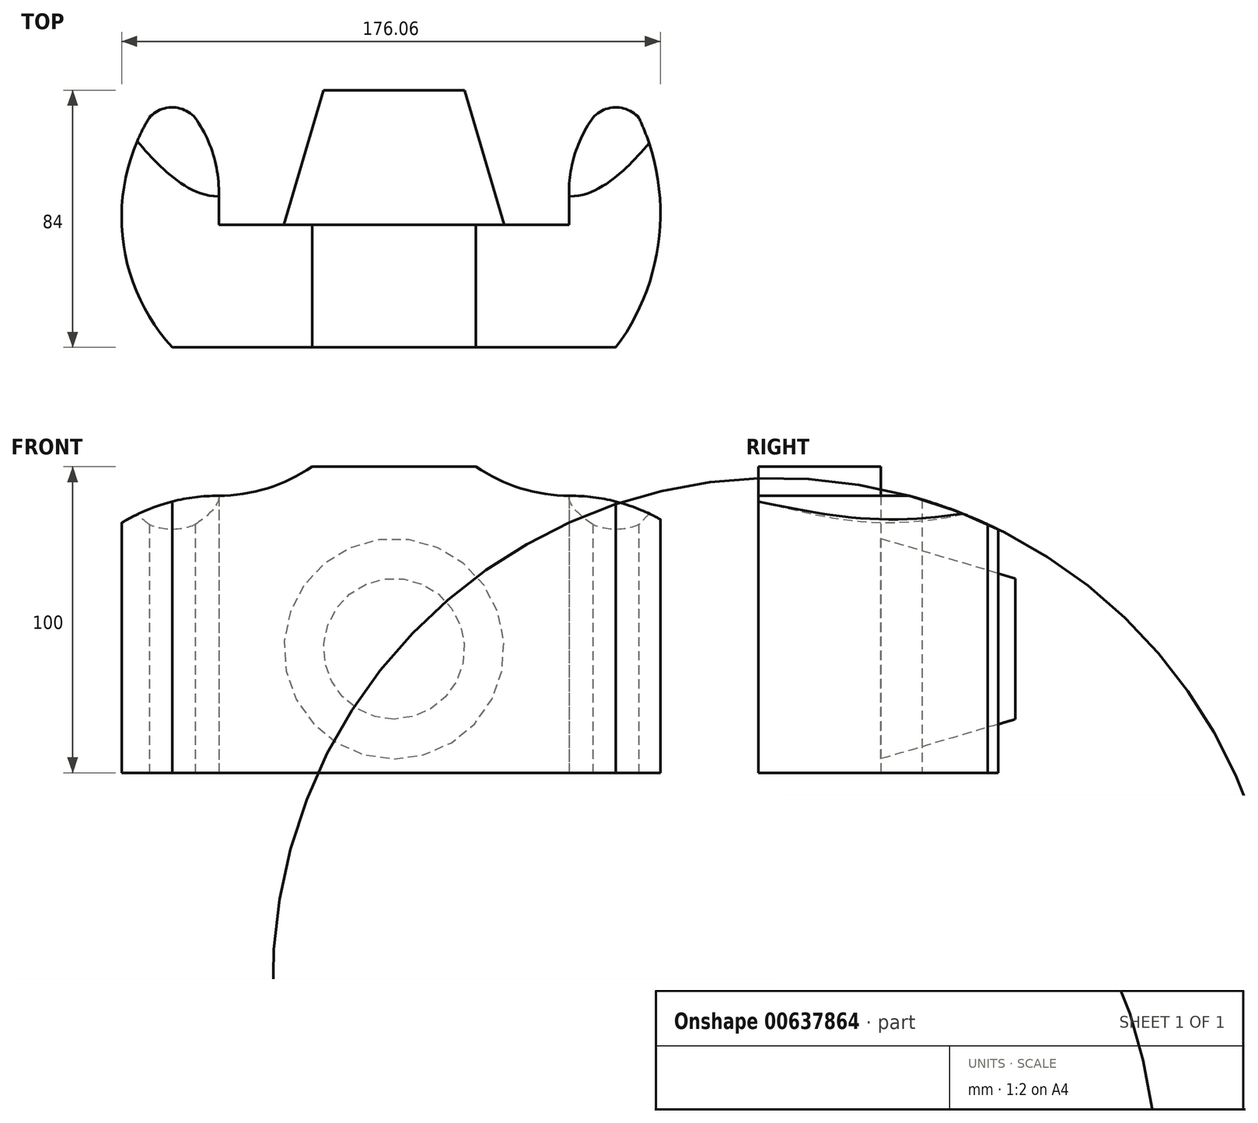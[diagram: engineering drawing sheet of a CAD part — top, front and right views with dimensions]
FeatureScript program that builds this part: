
annotation { "Feature Type Name" : "Feature", "Feature Type Description" : "" }
export const myFeature = defineFeature(function(context is Context, id is Id, definition is map)
    precondition{}
    {
        {
            var Q0;
            Q0=qCreatedBy(makeId("Top.planeOp"),FACE);
            var sketch = newSketch(context, id + "F0", { "sketchPlane" : qUnion([Q0])});
            skLineSegment(sketch, "E0.bottom", {"start": v(72.5, 20) * mm, "end": v(-72.5, 20) * mm, "construction": true});
            skLineSegment(sketch, "E0.top", {"start": v(72.5, -20) * mm, "end": v(-72.5, -20) * mm, "construction": true});
            skLineSegment(sketch, "E0.left", {"start": v(72.5, 20) * mm, "end": v(72.5, -20) * mm, "construction": true});
            skLineSegment(sketch, "E0.right", {"start": v(-72.5, 20) * mm, "end": v(-72.5, -20) * mm, "construction": true});
            skPoint(sketch, "E0.middle", {"position": v(0, 0) * mm});
            skLineSegment(sketch, "E1.bottom", {"start": v(25, 20) * mm, "end": v(-25, 20) * mm, "construction": true});
            skLineSegment(sketch, "E1.top", {"start": v(25, 20) * mm, "end": v(-25, 20) * mm, "construction": true});
            skLineSegment(sketch, "E1.left", {"start": v(25, 20) * mm, "end": v(25, 20) * mm});
            skLineSegment(sketch, "E1.right", {"start": v(-25, 20) * mm, "end": v(-25, 20) * mm});
            skPoint(sketch, "E1.middle", {"position": v(0, 20) * mm});
            skLineSegment(sketch, "E2", {"start": v(72.5, -20) * mm, "end": v(-72.5, -20) * mm});
            skLineSegment(sketch, "E3", {"start": v(-72.5, -20) * mm, "end": v(-72.5, 55) * mm, "construction": true});
            skLineSegment(sketch, "E4.bottom", {"start": v(-80, 55) * mm, "end": v(-65, 55) * mm, "construction": true});
            skLineSegment(sketch, "E4.top", {"start": v(-80, 20) * mm, "end": v(-65, 20) * mm, "construction": true});
            skLineSegment(sketch, "E4.left", {"start": v(-80, 55) * mm, "end": v(-80, 20) * mm, "construction": true});
            skLineSegment(sketch, "E4.right", {"start": v(-65, 55) * mm, "end": v(-65, 20) * mm, "construction": true});
            skArc(sketch, "E5", {"start": v(-80, 55) * mm, "mid": v(-88.7, 16.25) * mm, "end": v(-72.5, -20) * mm});
            skArc(sketch, "E6", {"start": v(-65, 55) * mm, "mid": v(-72.5, 58.39) * mm, "end": v(-80, 55) * mm});
            skArc(sketch, "E7", {"start": v(-57.25, 30.7) * mm, "mid": v(-59.23, 43.45) * mm, "end": v(-65, 55) * mm});
            skLineSegment(sketch, "E8", {"start": v(-57.25, 30.7) * mm, "end": v(-57.25, 20) * mm});
            skLineSegment(sketch, "E9", {"start": v(-57.25, 20) * mm, "end": v(52.26, 20) * mm});
            skLineSegment(sketch, "E10", {"start": v(72.5, -20) * mm, "end": v(72.5, 55) * mm, "construction": true});
            skLineSegment(sketch, "E11.bottom", {"start": v(65, 55) * mm, "end": v(80, 55) * mm, "construction": true});
            skLineSegment(sketch, "E11.top", {"start": v(65, 20) * mm, "end": v(80, 20) * mm, "construction": true});
            skLineSegment(sketch, "E11.left", {"start": v(65, 55) * mm, "end": v(65, 20) * mm, "construction": true});
            skLineSegment(sketch, "E11.right", {"start": v(80, 55) * mm, "end": v(80, 20) * mm, "construction": true});
            skArc(sketch, "E12", {"start": v(72.5, -20) * mm, "mid": v(86.68, 16.46) * mm, "end": v(80, 55) * mm});
            skArc(sketch, "E13", {"start": v(80, 55) * mm, "mid": v(72.5, 58.39) * mm, "end": v(65, 55) * mm});
            skArc(sketch, "E14", {"start": v(65, 55) * mm, "mid": v(59.63, 44.75) * mm, "end": v(57.25, 33.43) * mm});
            skLineSegment(sketch, "E15", {"start": v(57.25, 33.43) * mm, "end": v(57.25, 20) * mm});
            skLineSegment(sketch, "E16", {"start": v(57.25, 20) * mm, "end": v(-57.25, 20) * mm});
            skSolve(sketch);
        }
        {
            var Q0;
            Q0 = qSketchRegion(id + "F0", true);
            extrude(context, id + "F1", {"entities" : qUnion([Q0]), "depth" : 100 * mm, "offsetDistance" : 25 * mm});
        }
        {
            var Q0;
            Q0=makeQuery(id+"F1.opExtrude","SWEPT_FACE",FACE,{"disambiguationData":[OSD([sQuery(id+"F0.wireOp",EDGE,"E2")])]});
            var sketch = newSketch(context, id + "F2", { "sketchPlane" : qUnion([Q0])});
            skLineSegment(sketch, "E17", {"start": v(0, 100) * mm, "end": v(0, 81) * mm, "construction": true});
            skPoint(sketch, "E17.endSnap0", {"position": v(0, 100) * mm});
            skLineSegment(sketch, "E18.bottom", {"start": v(90.02, 81) * mm, "end": v(-90.02, 81) * mm, "construction": true});
            skLineSegment(sketch, "E18.top", {"start": v(90.02, 81) * mm, "end": v(-90.02, 81) * mm, "construction": true});
            skLineSegment(sketch, "E18.left", {"start": v(90.02, 81) * mm, "end": v(90.02, 81) * mm});
            skLineSegment(sketch, "E18.right", {"start": v(-90.02, 81) * mm, "end": v(-90.02, 81) * mm});
            skPoint(sketch, "E18.middle", {"position": v(0, 81) * mm});
            skLineSegment(sketch, "E19.bottom", {"start": v(26.78, 100) * mm, "end": v(-26.78, 100) * mm});
            skLineSegment(sketch, "E19.top", {"start": v(26.78, 100) * mm, "end": v(-26.78, 100) * mm});
            skLineSegment(sketch, "E19.left", {"start": v(26.78, 100) * mm, "end": v(26.78, 100) * mm});
            skLineSegment(sketch, "E19.right", {"start": v(-26.78, 100) * mm, "end": v(-26.78, 100) * mm});
            skLineSegment(sketch, "E20.bottom", {"start": v(57.43, 90.5) * mm, "end": v(-57.43, 90.5) * mm, "construction": true});
            skLineSegment(sketch, "E20.top", {"start": v(57.43, 90.5) * mm, "end": v(-57.43, 90.5) * mm, "construction": true});
            skLineSegment(sketch, "E20.left", {"start": v(57.43, 90.5) * mm, "end": v(57.43, 90.5) * mm});
            skLineSegment(sketch, "E20.right", {"start": v(-57.43, 90.5) * mm, "end": v(-57.43, 90.5) * mm});
            skPoint(sketch, "E20.middle", {"position": v(0, 90.5) * mm});
            skPoint(sketch, "E20.cornerSnap0", {"position": v(0, 90.5) * mm});
            skArc(sketch, "E21", {"start": v(-57.43, 90.5) * mm, "mid": v(-41.38, 92.93) * mm, "end": v(-26.78, 100) * mm});
            skArc(sketch, "E22", {"start": v(26.78, 100) * mm, "mid": v(41.38, 92.93) * mm, "end": v(57.43, 90.5) * mm});
            skArc(sketch, "E23", {"start": v(-57.43, 90.5) * mm, "mid": v(-74.4, 88.08) * mm, "end": v(-90.02, 81) * mm});
            skArc(sketch, "E24", {"start": v(90.02, 81) * mm, "mid": v(74.4, 88.08) * mm, "end": v(57.43, 90.5) * mm});
            skLineSegment(sketch, "E25", {"start": v(26.78, 100) * mm, "end": v(90.44, 100) * mm});
            skLineSegment(sketch, "E26", {"start": v(90.44, 100) * mm, "end": v(90.02, 81) * mm});
            skLineSegment(sketch, "E27", {"start": v(-26.78, 100) * mm, "end": v(-94.07, 100) * mm});
            skLineSegment(sketch, "E28", {"start": v(-94.07, 100) * mm, "end": v(-90.02, 81) * mm});
            skSolve(sketch);
        }
        {
            var Q0;
            Q0 = qSketchRegion(id + "F2", true);
            extrude(context, id + "F3", {"entities" : qUnion([Q0]), "operationType" : NewBodyOperationType.REMOVE, "oppositeDirection" : true, "depth" : 98.6 * mm, "offsetDistance" : 25 * mm});
        }
        {
            var Q0;
            Q0=qCreatedBy(makeId("Right.planeOp"),FACE);
            var sketch = newSketch(context, id + "F4", { "sketchPlane" : qUnion([Q0])});
            skLineSegment(sketch, "E29", {"start": v(66.75, 75.1) * mm, "end": v(66.75, 98.7) * mm});
            skLineSegment(sketch, "E30", {"start": v(66.75, 98.7) * mm, "end": v(24.8, 98.7) * mm});
            skLineSegment(sketch, "E31", {"start": v(24.8, 98.7) * mm, "end": v(24.8, 91.66) * mm});
            skArc(sketch, "E32", {"start": v(66.75, 75.1) * mm, "mid": v(46.35, 84.83) * mm, "end": v(24.8, 91.66) * mm});
            skSolve(sketch);
        }
        {
            var Q0;
            Q0 = qSketchRegion(id + "F4", true);
            extrude(context, id + "F5", {"entities" : qUnion([Q0]), "operationType" : NewBodyOperationType.REMOVE, "oppositeDirection" : true, "depth" : 90.4 * mm, "offsetDistance" : 25 * mm, "hasSecondDirection" : true, "secondDirectionOppositeDirection" : false, "secondDirectionDepth" : 126 * mm});
        }
        {
            var Q0;
            Q0=makeQuery(id+"F1.opExtrude","SWEPT_FACE",FACE,{"disambiguationData":[OSD([sQuery(id+"F0.wireOp",EDGE,"E16")])]});
            var sketch = newSketch(context, id + "F6", { "sketchPlane" : qUnion([Q0])});
            skLineSegment(sketch, "E33.bottom", {"start": v(30.57, 119) * mm, "end": v(-30.57, 119) * mm, "construction": true});
            skLineSegment(sketch, "E33.top", {"start": v(30.57, 81) * mm, "end": v(-30.57, 81) * mm, "construction": true});
            skLineSegment(sketch, "E33.left", {"start": v(30.57, 119) * mm, "end": v(30.57, 81) * mm, "construction": true});
            skLineSegment(sketch, "E33.right", {"start": v(-30.57, 119) * mm, "end": v(-30.57, 81) * mm, "construction": true});
            skPoint(sketch, "E33.middle", {"position": v(0, 100) * mm});
            skLineSegment(sketch, "E34", {"start": v(0, 81) * mm, "end": v(0, 0) * mm, "construction": true});
            skCircle(sketch, "E35", {"center": v(0, 40.5) * mm, "radius": 35.97 * mm});
            skSolve(sketch);
        }
        {
            var Q0;
            Q0=makeQuery(id+"F6.imprint","IMPRINT",FACE,{"disambiguationData":[TD([[makeQuery(id+"F6.imprint","IMPRINT",EDGE,{"derivedFrom":sQuery(id+"F6.wireOp",EDGE,"E35")}),1.0]])]});
            var sketch = newSketch(context, id + "F7", { "sketchPlane" : qUnion([Q0])});
            skCircle(sketch, "E36", {"center": v(0, 40.5) * mm, "radius": 1.59 * mm});
            skSolve(sketch);
        }
        {
            var Q0;
            Q0 = qSketchRegion(id + "F7", true);
            extrude(context, id + "F8", {"entities" : qUnion([Q0]), "operationType" : NewBodyOperationType.ADD, "depth" : 43 * mm, "offsetDistance" : 25 * mm});
        }
        {
            var Q0;
            Q0=makeQuery(id+"F8.opExtrude","CAP_FACE",FACE,{"disambiguationData":[OSD([sQuery(id+"F7.wireOp",EDGE,"E36")])],"isStart":false});
            var sketch = newSketch(context, id + "F9", { "sketchPlane" : qUnion([Q0])});
            skCircle(sketch, "E37", {"center": v(0, 40.5) * mm, "radius": 23 * mm});
            skSolve(sketch);
        }
        {
            var Q0;
            Q0 = qSketchRegion(id + "F9", true);
            extrude(context, id + "F10", {"entities" : qUnion([Q0]), "operationType" : NewBodyOperationType.ADD, "depth" : 1 * mm, "offsetDistance" : 25 * mm});
        }
        {
            var Q1;
            Q1=makeQuery(id+"F10.opExtrude","CAP_FACE",FACE,{"disambiguationData":[OSD([sQuery(id+"F9.wireOp",EDGE,"E37")])],"isStart":false});
            var Q2;
            Q2 = qSketchRegion(id + "F6", true);
            loft(context, id + "F11", {"operationType" : NewBodyOperationType.ADD, "sheetProfilesArray" : [{ "sheetProfileEntities" : qUnion([Q1]) }, { "sheetProfileEntities" : qUnion([Q2]) }]});
        }
    });
